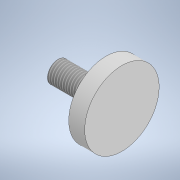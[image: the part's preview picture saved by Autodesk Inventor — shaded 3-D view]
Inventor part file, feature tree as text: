
AUTODESK INVENTOR PART (.ipt)
format: ipt  version: 2022 (Build 260153000, 153)  size: 110,592 bytes
history: native  units: mm
features: revolve x1, thread x1, sketch x1
ambient origin geometry x8: Origin, YZ Plane, XZ Plane, XY Plane, X Axis, Y Axis, Z Axis, Center Point
bodies: Solid1 (feature_tree)
feature tree (3):
  revolve  "Revolution1"  [1 undecoded]
  thread  "Thread1"  [1 undecoded]
  sketch  "Sketch1"  dims[d4=10.0mm d5=35.0mm d6=5.0mm d7=10.0mm d8=20.0mm d9=15.0mm d10=90.0deg d11=35.0mm d12=0.0mm]
note: 2 required parameter values undecoded (feature->parameter linkage not recoverable at this tier; creation-order binding heuristic only, values carry confidence <= 0.55)